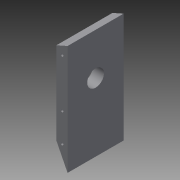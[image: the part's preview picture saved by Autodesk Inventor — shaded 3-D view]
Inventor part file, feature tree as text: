
AUTODESK INVENTOR PART (.ipt)
format: ipt  version: 2015 (Build 190159000, 159)  size: 89,088 bytes
history: native  units: mm
features: sketch x2, extrude x2, plane x1
ambient origin geometry x8: Origin, YZ Plane, XZ Plane, XY Plane, X Axis, Y Axis, Z Axis, Center Point
bodies: Body1 (feature_tree)
feature tree (5):
  sketch  "Sketch1"  dims[d3=10.0mm d4=73.5mm]
  plane  "Work Plane1"
  sketch  "Sketch2"  dims[d6=4.444444mm d8=20.0mm d17=2.5mm d23=15.0mm d26=2.5mm d28=2.5mm d29=50.0mm d30=0.0mm d31=10.0mm d32=0.0mm]
  extrude  "Extrusion3"  Depth=10.0mm
  extrude  "Extrusion4"  Depth=10.0mm
